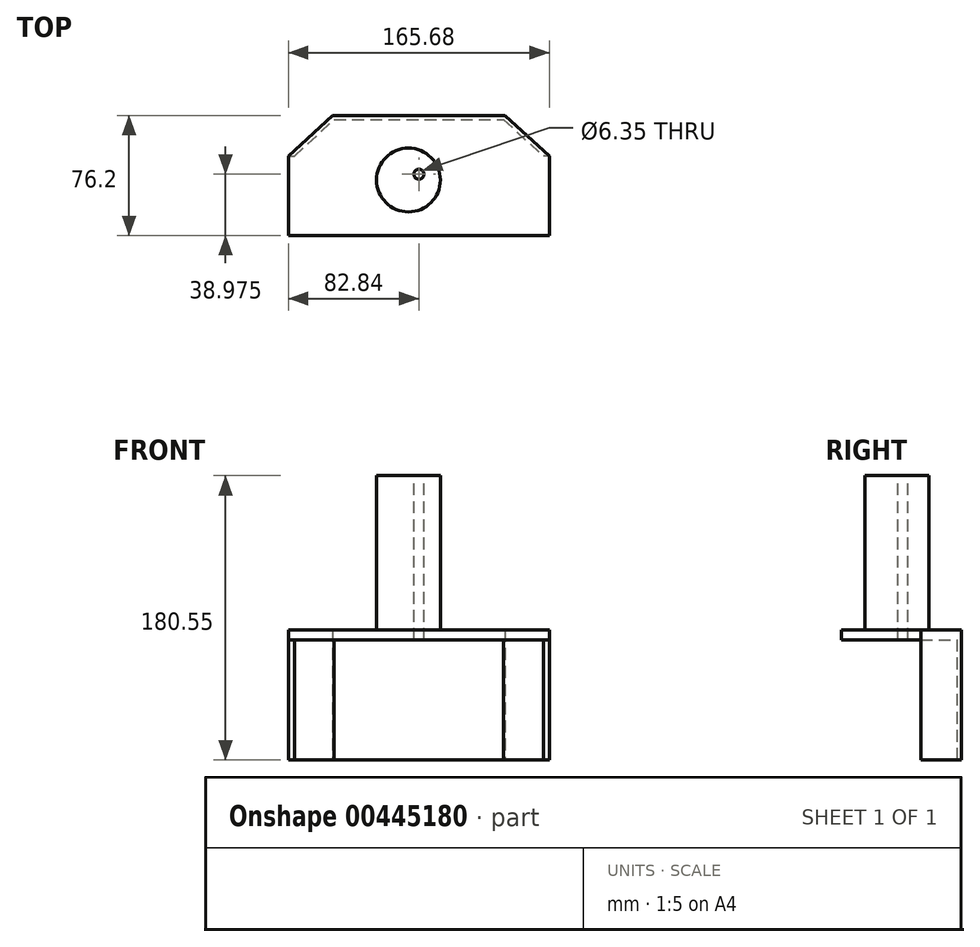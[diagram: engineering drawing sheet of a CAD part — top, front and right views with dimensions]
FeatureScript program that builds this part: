
annotation { "Feature Type Name" : "Feature", "Feature Type Description" : "" }
export const myFeature = defineFeature(function(context is Context, id is Id, definition is map)
    precondition{}
    {
        {
            var Q0;
            Q0=qCreatedBy(makeId("Top.planeOp"),FACE);
            var sketch = newSketch(context, id + "F0", { "sketchPlane" : qUnion([Q0])});
            skLineSegment(sketch, "E0", {"start": v(-82.84, 0) * mm, "end": v(82.84, 0) * mm});
            skLineSegment(sketch, "E1", {"start": v(-82.84, 0) * mm, "end": v(-82.84, 50.36) * mm});
            skLineSegment(sketch, "E2", {"start": v(-82.84, 50.36) * mm, "end": v(-54.84, 76.2) * mm});
            skLineSegment(sketch, "E3", {"start": v(-54.84, 76.2) * mm, "end": v(54.84, 76.2) * mm});
            skLineSegment(sketch, "E4", {"start": v(54.84, 76.2) * mm, "end": v(82.84, 50.36) * mm});
            skLineSegment(sketch, "E5", {"start": v(82.84, 50.36) * mm, "end": v(82.84, 0) * mm});
            skSolve(sketch);
        }
        {
            var Q0;
            Q0 = qSketchRegion(id + "F0", true);
            extrude(context, id + "F1", {"entities" : qUnion([Q0]), "depth" : 6.35 * mm});
        }
        {
            var Q0;
            Q0=makeQuery(id+"F1.opExtrude","CAP_FACE",FACE,{"disambiguationData":[OSD([sQuery(id+"F0.wireOp",EDGE,"E0"),sQuery(id+"F0.wireOp",EDGE,"E1"),sQuery(id+"F0.wireOp",EDGE,"E2"),sQuery(id+"F0.wireOp",EDGE,"E3"),sQuery(id+"F0.wireOp",EDGE,"E4"),sQuery(id+"F0.wireOp",EDGE,"E5")])],"isStart":true});
            var sketch = newSketch(context, id + "F2", { "sketchPlane" : qUnion([Q0])});
            skLineSegment(sketch, "E6.0", {"start": v(54.84, -76.2) * mm, "end": v(82.84, -50.36) * mm});
            skLineSegment(sketch, "E6.1", {"start": v(-54.84, -76.2) * mm, "end": v(54.84, -76.2) * mm});
            skLineSegment(sketch, "E6.2", {"start": v(-82.84, -50.36) * mm, "end": v(-54.84, -76.2) * mm});
            skLineSegment(sketch, "E7.0", {"start": v(53.85, -73.66) * mm, "end": v(79.1, -50.36) * mm});
            skLineSegment(sketch, "E7.1", {"start": v(-53.85, -73.66) * mm, "end": v(53.85, -73.66) * mm});
            skLineSegment(sketch, "E7.2", {"start": v(-79.1, -50.36) * mm, "end": v(-53.85, -73.66) * mm});
            skLineSegment(sketch, "E8", {"start": v(-82.84, -50.36) * mm, "end": v(-79.1, -50.36) * mm});
            skLineSegment(sketch, "E9", {"start": v(82.84, -50.36) * mm, "end": v(79.1, -50.36) * mm});
            skSolve(sketch);
        }
        {
            var Q0;
            Q0 = qSketchRegion(id + "F2", true);
            extrude(context, id + "F3", {"entities" : qUnion([Q0]), "operationType" : NewBodyOperationType.ADD, "depth" : 76.2 * mm});
        }
        {
            var Q0;
            Q0=makeQuery(id+"F1.opExtrude","CAP_FACE",FACE,{"disambiguationData":[OSD([sQuery(id+"F0.wireOp",EDGE,"E0"),sQuery(id+"F0.wireOp",EDGE,"E1"),sQuery(id+"F0.wireOp",EDGE,"E2"),sQuery(id+"F0.wireOp",EDGE,"E3"),sQuery(id+"F0.wireOp",EDGE,"E4"),sQuery(id+"F0.wireOp",EDGE,"E5")])],"isStart":true});
            var sketch = newSketch(context, id + "F4", { "sketchPlane" : qUnion([Q0])});
            skCircle(sketch, "E10", {"center": v(-6.62, -35.3) * mm, "radius": 20.27 * mm});
            skSolve(sketch);
        }
        {
            var Q0;
            Q0 = qSketchRegion(id + "F4", true);
            extrude(context, id + "F5", {"entities" : qUnion([Q0]), "operationType" : NewBodyOperationType.ADD, "oppositeDirection" : true, "depth" : 104.35 * mm});
        }
        {
            var Q0;
            Q0=makeQuery(id+"F5.opExtrude","CAP_FACE",FACE,{"disambiguationData":[OSD([sQuery(id+"F4.wireOp",EDGE,"E10")])],"isStart":false});
            var sketch = newSketch(context, id + "F6", { "sketchPlane" : qUnion([Q0])});
            skCircle(sketch, "E11", {"center": v(0, 38.98) * mm, "radius": 3.18 * mm});
            skSolve(sketch);
        }
        {
            var Q0;
            Q0 = qSketchRegion(id + "F6", true);
            extrude(context, id + "F7", {"entities" : qUnion([Q0]), "operationType" : NewBodyOperationType.REMOVE, "endBound" : BoundingType.THROUGH_ALL, "oppositeDirection" : true, "depth" : 25.4 * mm});
        }
    });
